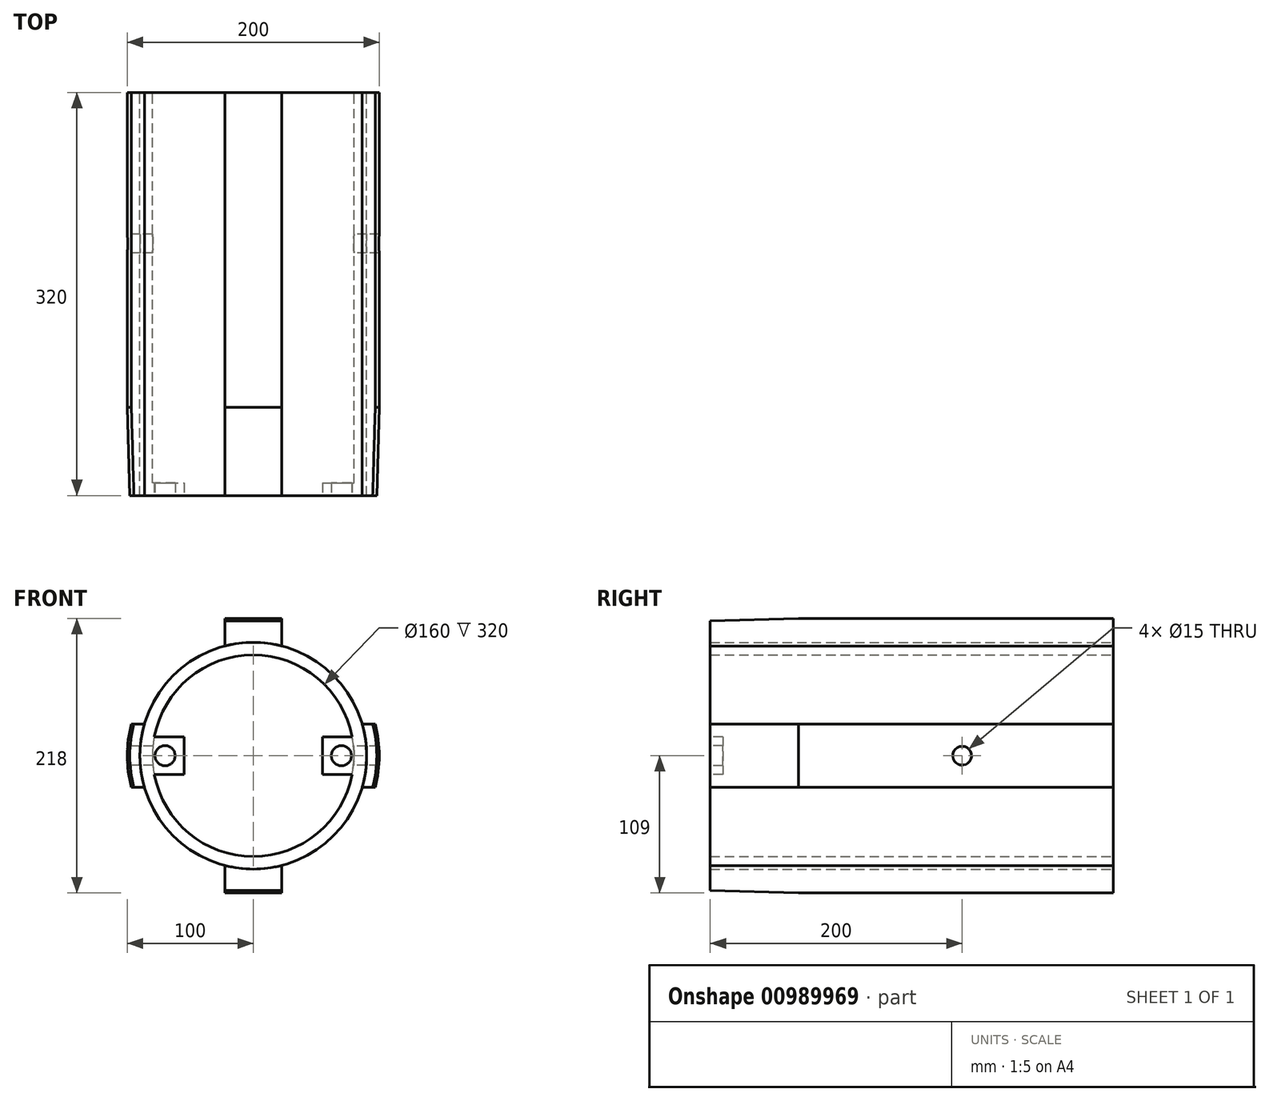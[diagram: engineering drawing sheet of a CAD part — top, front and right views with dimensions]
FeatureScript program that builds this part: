
annotation { "Feature Type Name" : "Feature", "Feature Type Description" : "" }
export const myFeature = defineFeature(function(context is Context, id is Id, definition is map)
    precondition{}
    {
        {
            var Q0;
            Q0=qCreatedBy(makeId("Front.planeOp"),FACE);
            var sketch = newSketch(context, id + "F0", { "sketchPlane" : qUnion([Q0])});
            skArc(sketch, "E0", {"start": v(-96.82, 25) * mm, "mid": v(-100, 0) * mm, "end": v(-96.82, -25) * mm});
            skCircle(sketch, "E1", {"center": v(0, 0) * mm, "radius": 90 * mm});
            skCircle(sketch, "E2", {"center": v(0, 0) * mm, "radius": 80 * mm});
            skLineSegment(sketch, "E3.bottom", {"start": v(-96.82, 25) * mm, "end": v(-86.46, 25) * mm});
            skLineSegment(sketch, "E3.top", {"start": v(-96.82, -25) * mm, "end": v(-86.46, -25) * mm});
            skArc(sketch, "E4.trimOffspring", {"start": v(96.82, -25) * mm, "mid": v(100, 0) * mm, "end": v(96.82, 25) * mm});
            skLineSegment(sketch, "E5.bottom", {"start": v(-22.5, 109) * mm, "end": v(22.5, 109) * mm});
            skLineSegment(sketch, "E5.top", {"start": v(-22.5, -109) * mm, "end": v(22.5, -109) * mm});
            skLineSegment(sketch, "E5.left", {"start": v(-22.5, 109) * mm, "end": v(-22.5, 87.14) * mm});
            skLineSegment(sketch, "E5.right", {"start": v(22.5, 109) * mm, "end": v(22.5, 87.14) * mm});
            skLineSegment(sketch, "E6.trimOffspring", {"start": v(86.46, -25) * mm, "end": v(96.82, -25) * mm});
            skLineSegment(sketch, "E7.trimOffspring", {"start": v(-22.5, -87.14) * mm, "end": v(-22.5, -109) * mm});
            skLineSegment(sketch, "E8.trimOffspring", {"start": v(22.5, -87.14) * mm, "end": v(22.5, -109) * mm});
            skLineSegment(sketch, "E9.trimOffspring", {"start": v(86.46, 25) * mm, "end": v(96.82, 25) * mm});
            skSolve(sketch);
        }
        {
            var Q0;
            {var subQ4=sQuery(id+"F0.wireOp",EDGE,"E3.bottom");var subQ5=sQuery(id+"F0.wireOp",EDGE,"E1");var subQ6=makeQuery(id+"F0.imprint","INTERSECT",VERTEX,{"disambiguationData":[OD(1.0)],"derivedFrom":[subQ5,subQ4]});Q0=makeQuery(id+"F0.imprint","IMPRINT",FACE,{"disambiguationData":[TD([[makeQuery(id+"F0.imprint","IMPRINT",EDGE,{"disambiguationData":[TD([[subQ6,-1.0]])],"derivedFrom":subQ5}),1.0]])]});}
            var Q1;
            {var subQ0=sQuery(id+"F0.wireOp",EDGE,"6BsrhhA7-Mifx-Ozz0-bhCS-hr22MbMvMuD0.right");var subQ1=sQuery(id+"F0.wireOp",EDGE,"E1");var subQ2=makeQuery(id+"F0.imprint","INTERSECT",VERTEX,{"disambiguationData":[OD(0.0)],"derivedFrom":[subQ1,subQ0]});Q1=makeQuery(id+"F0.imprint","IMPRINT",FACE,{"disambiguationData":[TD([[makeQuery(id+"F0.imprint","IMPRINT",EDGE,{"disambiguationData":[TD([[subQ2,1.0]])],"derivedFrom":subQ1}),1.0]])]});}
            var Q2;
            {var subQ0=sQuery(id+"F0.wireOp",EDGE,"6BsrhhA7-Mifx-Ozz0-bhCS-hr22MbMvMuD0.left");var subQ1=sQuery(id+"F0.wireOp",EDGE,"E1");var subQ2=makeQuery(id+"F0.imprint","INTERSECT",VERTEX,{"disambiguationData":[OD(0.0)],"derivedFrom":[subQ1,subQ0]});Q2=makeQuery(id+"F0.imprint","IMPRINT",FACE,{"disambiguationData":[TD([[makeQuery(id+"F0.imprint","IMPRINT",EDGE,{"disambiguationData":[TD([[subQ2,-1.0]])],"derivedFrom":subQ1}),1.0]])]});}
            var Q3;
            {var subQ0=sQuery(id+"F0.wireOp",EDGE,"6BsrhhA7-Mifx-Ozz0-bhCS-hr22MbMvMuD0.right");var subQ1=sQuery(id+"F0.wireOp",EDGE,"E1");var subQ2=makeQuery(id+"F0.imprint","INTERSECT",VERTEX,{"disambiguationData":[OD(1.0)],"derivedFrom":[subQ1,subQ0]});Q3=makeQuery(id+"F0.imprint","IMPRINT",FACE,{"disambiguationData":[TD([[makeQuery(id+"F0.imprint","IMPRINT",EDGE,{"disambiguationData":[TD([[subQ2,-1.0]])],"derivedFrom":subQ1}),1.0]])]});}
            var Q4;
            {var subQ0=sQuery(id+"F0.wireOp",EDGE,"6BsrhhA7-Mifx-Ozz0-bhCS-hr22MbMvMuD0.right");var subQ1=sQuery(id+"F0.wireOp",EDGE,"E1");var subQ2=makeQuery(id+"F0.imprint","INTERSECT",VERTEX,{"disambiguationData":[OD(0.0)],"derivedFrom":[subQ1,subQ0]});Q4=makeQuery(id+"F0.imprint","IMPRINT",FACE,{"disambiguationData":[TD([[makeQuery(id+"F0.imprint","IMPRINT",EDGE,{"disambiguationData":[TD([[subQ2,-1.0]])],"derivedFrom":subQ1}),1.0]])]});}
            var Q5;
            {var subQ0=sQuery(id+"F0.wireOp",EDGE,"6BsrhhA7-Mifx-Ozz0-bhCS-hr22MbMvMuD0.left");var subQ1=sQuery(id+"F0.wireOp",EDGE,"E1");var subQ2=makeQuery(id+"F0.imprint","INTERSECT",VERTEX,{"disambiguationData":[OD(1.0)],"derivedFrom":[subQ1,subQ0]});Q5=makeQuery(id+"F0.imprint","IMPRINT",FACE,{"disambiguationData":[TD([[makeQuery(id+"F0.imprint","IMPRINT",EDGE,{"disambiguationData":[TD([[subQ2,-1.0]])],"derivedFrom":subQ1}),1.0]])]});}
            var Q6;
            {var subQ3=sQuery(id+"F0.wireOp",EDGE,"E3.bottom");var subQ7=sQuery(id+"F0.wireOp",EDGE,"E1");var subQ8=makeQuery(id+"F0.imprint","INTERSECT",VERTEX,{"disambiguationData":[OD(0.0)],"derivedFrom":[subQ7,subQ3]});Q6=makeQuery(id+"F0.imprint","IMPRINT",FACE,{"disambiguationData":[TD([[makeQuery(id+"F0.imprint","IMPRINT",EDGE,{"disambiguationData":[TD([[subQ8,1.0]])],"derivedFrom":subQ7}),1.0]])]});}
            var Q7;
            {var subQ0=sQuery(id+"F0.wireOp",EDGE,"E3.top");var subQ1=sQuery(id+"F0.wireOp",EDGE,"E1");var subQ2=makeQuery(id+"F0.imprint","INTERSECT",VERTEX,{"disambiguationData":[OD(0.0)],"derivedFrom":[subQ1,subQ0]});Q7=makeQuery(id+"F0.imprint","IMPRINT",FACE,{"disambiguationData":[TD([[makeQuery(id+"F0.imprint","IMPRINT",EDGE,{"disambiguationData":[TD([[subQ2,-1.0]])],"derivedFrom":subQ1}),1.0]])]});}
            extrude(context, id + "F1", {"entities" : qUnion([Q0, Q1, Q2, Q3, Q4, Q5, Q6, Q7]), "depth" : 320 * mm, "offsetDistance" : 25 * mm});
        }
        {
            var Q0;
            {var subQ0=sQuery(id+"F0.wireOp",EDGE,"E0");Q0=makeQuery(id+"F0.imprint","IMPRINT",FACE,{"disambiguationData":[TD([[makeQuery(id+"F0.imprint","IMPRINT",EDGE,{"derivedFrom":subQ0}),1.0]])]});}
            var Q1;
            {var subQ5=sQuery(id+"F0.wireOp",EDGE,"85f4570a-dc56-4e68-8341-b73cf04247c9.trimOffspring");Q1=makeQuery(id+"F0.imprint","IMPRINT",FACE,{"disambiguationData":[TD([[makeQuery(id+"F0.imprint","IMPRINT",EDGE,{"derivedFrom":subQ5}),1.0]])]});}
            var Q2;
            {var subQ5=sQuery(id+"F0.wireOp",EDGE,"E4.trimOffspring");Q2=makeQuery(id+"F0.imprint","IMPRINT",FACE,{"disambiguationData":[TD([[makeQuery(id+"F0.imprint","IMPRINT",EDGE,{"derivedFrom":subQ5}),1.0]])]});}
            var Q3;
            {var subQ5=sQuery(id+"F0.wireOp",EDGE,"fc8958ad-76b3-43b6-b9b7-f53bbd31248f.trimOffspring");Q3=makeQuery(id+"F0.imprint","IMPRINT",FACE,{"disambiguationData":[TD([[makeQuery(id+"F0.imprint","IMPRINT",EDGE,{"derivedFrom":subQ5}),1.0]])]});}
            var Q4;
            Q4=makeQuery(id+"F0.imprint","IMPRINT",FACE,{"disambiguationData":[TD([[makeQuery(id+"F0.imprint","IMPRINT",EDGE,{"derivedFrom":sQuery(id+"F0.wireOp",EDGE,"E5.bottom")}),-1.0]])]});
            var Q5;
            Q5=makeQuery(id+"F0.imprint","IMPRINT",FACE,{"disambiguationData":[TD([[makeQuery(id+"F0.imprint","IMPRINT",EDGE,{"derivedFrom":sQuery(id+"F0.wireOp",EDGE,"E5.top")}),1.0]])]});
            extrude(context, id + "F2", {"entities" : qUnion([Q0, Q1, Q2, Q3, Q4, Q5]), "depth" : 320 * mm, "offsetDistance" : 25 * mm});
        }
        {
            var Q0;
            Q0=makeQuery(id+"F2.opExtrude","CAP_EDGE",EDGE,{"disambiguationData":[OSD([sQuery(id+"F0.wireOp",EDGE,"E4.trimOffspring")])],"isStart":false});
            var Q1;
            Q1=makeQuery(id+"F2.opExtrude","CAP_EDGE",EDGE,{"disambiguationData":[OSD([sQuery(id+"F0.wireOp",EDGE,"E0")])],"isStart":false});
            chamfer(context, id + "F3", {"entities" : qUnion([Q0, Q1]), "chamferType" : ChamferType.TWO_OFFSETS, "width1" : 2 * mm, "oppositeDirection" : false, "width2" : 70 * mm, "tangentPropagation" : true});
        }
        {
            var Q0;
            Q0=makeQuery(id+"F2.opExtrude","CAP_EDGE",EDGE,{"disambiguationData":[OSD([sQuery(id+"F0.wireOp",EDGE,"E5.bottom")])],"isStart":false});
            chamfer(context, id + "F4", {"entities" : qUnion([Q0]), "chamferType" : ChamferType.TWO_OFFSETS, "width1" : 70 * mm, "oppositeDirection" : false, "width2" : 2 * mm, "tangentPropagation" : true});
        }
        {
            var Q0;
            Q0=qCreatedBy(makeId("Right.planeOp"),FACE);
            var sketch = newSketch(context, id + "F5", { "sketchPlane" : qUnion([Q0])});
            skLineSegment(sketch, "E10.bottom", {"start": v(0, 60) * mm, "end": v(-120, 60) * mm});
            skLineSegment(sketch, "E10.top", {"start": v(0, 0) * mm, "end": v(-120, 0) * mm});
            skLineSegment(sketch, "E10.left", {"start": v(0, 60) * mm, "end": v(0, 0) * mm});
            skLineSegment(sketch, "E10.right", {"start": v(-120, 60) * mm, "end": v(-120, 0) * mm});
            skCircle(sketch, "E11", {"center": v(-120, 0) * mm, "radius": 7.5 * mm});
            skSolve(sketch);
        }
        {
            var Q0;
            {var subQ0=sQuery(id+"F5.wireOp",EDGE,"E10.right");var subQ1=sQuery(id+"F5.wireOp",EDGE,"E10.top");var subQ2=makeQuery(id+"F5.imprint","INTERSECT",VERTEX,{"derivedFrom":[subQ1,subQ0]});Q0=makeQuery(id+"F5.imprint","IMPRINT",FACE,{"disambiguationData":[TD([[makeQuery(id+"F5.imprint","IMPRINT",EDGE,{"disambiguationData":[TD([[subQ2,1.0]])],"derivedFrom":subQ1}),1.0]])]});}
            var Q1;
            {var subQ0=sQuery(id+"F5.wireOp",EDGE,"E10.right");var subQ1=sQuery(id+"F5.wireOp",EDGE,"E10.top");var subQ2=makeQuery(id+"F5.imprint","INTERSECT",VERTEX,{"derivedFrom":[subQ1,subQ0]});Q1=makeQuery(id+"F5.imprint","IMPRINT",FACE,{"disambiguationData":[TD([[makeQuery(id+"F5.imprint","IMPRINT",EDGE,{"disambiguationData":[TD([[subQ2,1.0]])],"derivedFrom":subQ1}),-1.0]])]});}
            var Q2;
            Q2=sQuery(id+"F5.wireOp",EDGE,"E11");
            extrude(context, id + "F6", {"entities" : qUnion([Q0, Q1]), "operationType" : NewBodyOperationType.REMOVE, "surfaceEntities" : qUnion([Q2]), "endBound" : BoundingType.SYMMETRIC, "depth" : 700 * mm, "offsetDistance" : 25 * mm});
        }
        {
            var Q0;
            Q0=qCreatedBy(makeId("Front.planeOp"),FACE);
            cPlane(context, id + "F7", {"entities" : qUnion([Q0]), "cplaneType" : CPlaneType.OFFSET, "offset" : 320 * mm, "width" : 150 * mm, "height" : 150 * mm});
        }
        {
            var Q0;
            Q0=qCreatedBy(id+"F7.planeOp",FACE);
            var sketch = newSketch(context, id + "F8", { "sketchPlane" : qUnion([Q0])});
            skLineSegment(sketch, "E12.bottom", {"start": v(-78.58, 15) * mm, "end": v(-55, 15) * mm});
            skLineSegment(sketch, "E12.top", {"start": v(-78.58, -15) * mm, "end": v(-55, -15) * mm});
            skLineSegment(sketch, "E13.left", {"start": v(-55, 15) * mm, "end": v(-55, -15) * mm});
            skLineSegment(sketch, "E13.right", {"start": v(55, 15) * mm, "end": v(55, -15) * mm});
            skCircle(sketch, "E14", {"center": v(-70, 0) * mm, "radius": 8 * mm});
            skCircle(sketch, "E15", {"center": v(70, 0) * mm, "radius": 8 * mm});
            skCircle(sketch, "E16", {"center": v(0, 0) * mm, "radius": 80 * mm});
            skLineSegment(sketch, "E17.trimOffspring", {"start": v(55, -15) * mm, "end": v(78.58, -15) * mm});
            skLineSegment(sketch, "E18.trimOffspring", {"start": v(55, 15) * mm, "end": v(78.58, 15) * mm});
            skSolve(sketch);
        }
        {
            var Q0;
            {var subQ1=sQuery(id+"F8.wireOp",EDGE,"E12.bottom");Q0=makeQuery(id+"F8.imprint","IMPRINT",FACE,{"disambiguationData":[TD([[makeQuery(id+"F8.imprint","IMPRINT",EDGE,{"derivedFrom":subQ1}),-1.0]])]});}
            var Q1;
            Q1=makeQuery(id+"F8.imprint","IMPRINT",FACE,{"disambiguationData":[TD([[makeQuery(id+"F8.imprint","IMPRINT",EDGE,{"derivedFrom":sQuery(id+"F8.wireOp",EDGE,"E13.right")}),1.0]])]});
            extrude(context, id + "F9", {"entities" : qUnion([Q0, Q1]), "operationType" : NewBodyOperationType.ADD, "oppositeDirection" : true, "depth" : 10 * mm, "offsetDistance" : 25 * mm});
        }
        {
            var Q0;
            Q0=makeQuery(id+"F2.opExtrude","CAP_EDGE",EDGE,{"disambiguationData":[OSD([sQuery(id+"F0.wireOp",EDGE,"E5.top")])],"isStart":false});
            chamfer(context, id + "F10", {"entities" : qUnion([Q0]), "chamferType" : ChamferType.TWO_OFFSETS, "width1" : 2 * mm, "oppositeDirection" : false, "width2" : 70 * mm, "tangentPropagation" : true});
        }
    });
